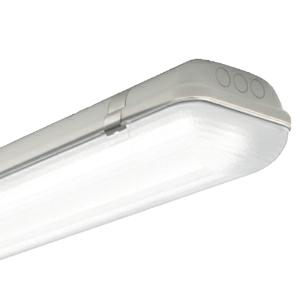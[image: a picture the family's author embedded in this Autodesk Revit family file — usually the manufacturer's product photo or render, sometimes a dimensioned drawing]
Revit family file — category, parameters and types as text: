
# Revit family: 3f_filippi_-_3f_linda_soft_3f_filippi_-_58754_-_3f_linda_led_soft_2x30w_dali_l1570
name_source: partatom
category: Lighting Fixtures
units: mm (PartAtom-declared; Revit-internal decimal feet)

## family parameters
Cut with Voids When Loaded = No
Host = Face
Light Source = No
Part Type = Normal
Room Calculation Point = No
Round Connector Dimension = Use Diameter
Shared = No

## types (1)
- 3F Filippi - 3F Linda Soft (1 x LED, 8788 lm, 66 W, 4000 K)
    Apparent Load = 66 VA
    Approval mark = CE
    CIE Flux Codes = 42 72 91 93 100
    Color Rendering = 80
    Color Temperature = 4000 K
    Control Gear = Electronic transformer
    Default Elevation = 1800 mm
    Description = ILLUMINOTECHNICAL
Luminous efficiency 100% (DLOR 93%, ULOR 7%).
Initial luminous flux of the luminaire 8788 lm.
Direct symmetric distribution.
Installation Interdistance Transv.D = 1.35 x hu - Long.D = 1.24 x hu.
Tabular UGR (CIE 117 - 4H-8H; S=0.25H; 70/50/20): RUG 24.5 - 22.7.
Beam angle: 131° - 111°.
Luminous efficacy 133 lm/W.
Lifetime (L93/B10): 30000 h. (tq+25°C)
Lifetime (L90/B10): 50000 h. (tq+25°C)
Lifetime (L85/B10): 80000 h. (tq+25°C)
Lifetime (L80/B10): 100000 h. (tq+25°C)
Lifetime (L85/B10): 50000 h. (tq+35°C)
Sudden decreased luminous flux after 50000 hours: 0% (C0).
Photobiological safety in compliance with IEC/TR 62778: RG0 risk exempt, (IEC 62471).
In compliance with IEC/EN 62722-2-1 - IEC/EN 62717 standards.

SOURCE
2 linear LED modules 30W/840.
Energy efficiency class (UE 2019/2020 - UE 2019/2015): D.
CIE 13.3 Colour rendering index: CRI >80 (R9 <50%).
IES TM-30 Fidelity Index: Rf = 84 Rg = 95.
CCT nominal colour temperature 4000 K.
Colour initial tolerance (MacAdam): SDCM 3.

MECHANICAL
Self-extinguishing V2 polycarbonate housing, injection moulded, RAL 7035 grey.
Ecologic anti-aging injected sealing gasket.
Soft opal diffuser in self-extinguishing V2 polycarbonate, photo-engraved interior, UV stabilised, injection moulded.
Gear-holder reflector in hot-dip galvanised steel, painted with white polyester base.
Snug fit safety snap-lock clips for diffuser mounting in stainless steel, screwdriver opening.
Fixing brackets in stainless steel.
Possibility for technicians to access the interior of the luminaire.
Luminaire with limited surface temperature. - D - (EN 60598-2-24)
Dimensions: 1570x160 mm, height 100 mm. Weight 3.35 kg.
IP66 protection degree.
Mechanical strength to impacts IK10 (20 joule).
Glow-wire test resistance 850°C.

ELECTRICAL
Halogen Free DALI-2 DATI (Parts 251, 252, 253), PUSH-DIM, electronic wiring 230V-50/60Hz, power factor 0.97 at full load, THD <25%, constant output current, SELV, class I, 1 driver, 1 DALI addresse.
Power of the luminaire 66 W.
ENEC - CE.
SAFE FLICKER: PstLM=<1 and SVM=<0.4 (IEC TR 61547-1 and IEC TR 63158), to ensure a more comfortable and safe light.
Luminaire compliant with EN 60598-2-22 for power supply from a centralised emergency system CPSS (Central Power Supply System), not incorporated in the luminaire - high risk areas excluded. The default power and flux are 100% in AC and 15% in DC.
Ambient temperature from -20°C to +35°C.
Temperature class T6 max 85°C.
Relative humidity UR: <85%.

INSTALLATION
Ceiling / Suspended / Wall.
All accessories dedicated to this product are available on the Catalog and on our website www.3F-Filippi.com.

APPLICATIONS
Suitable product for food production plants (HACCP), IFS (Food Version 6), BRC (GSFS Food Version 7).
Dry, dusty indoor environments, subject to occasional water splashes.
Luminaires designed for diffuse direct/indirect lighting suitable to provide optimum visual comfort.
Transit areas, stairwells.
Virtually shatterproof polycarbonate compatibly with the fumes / atmospheres that compromise the elasticity of plastic materials.
Suitable for illumination of public car parks and parking grounds referred to DIN 67528:2018-04.

LIGHT MANAGEMENT
Recommended minimum setting: 10%.
The luminaire, equipped with (DALI-2 DATI) driver, can be controlled manually with 3F Easy Dim technology or automatically/manually with wired or wireless DALI/D2D control systems.
The D2D driver guarantees interoperability with other devices with the same certification by making the following information available:
Device Data (Part 251), Energy Report (Part 252), Diagnosis & Maintenance (Part 253).
In electrical systems without a regulation system (manual or automatic) and DALI bus, a suitable jumper must be made on the DA-DA terminals of the appliance.

WARNING
Fixture not suitable for cold stores with an ambient temperature <0°C and/or relative humidity >85%.
Luminaire designed for disposal/recycling at end-of-life.
Replaceable (LED only) light source by a professional. Replaceable control gear by a professional.
    Height = 100 mm  [stored 0.328084 ft]
    Lamp = 1 x LED
    Lamp Light Flux = 8788 lm
    Lamp Power = 66 W
    Lamp count = 1
    Length = 1570 mm
    Lifetime = 50000 h
    Luminous efficacy = 133 lm/W
    Manufacturer = 3F Filippi
    ModVariant = No
    Model = 3F Filippi - 58754 - 3F Linda LED Soft 2x30W DALI L1570
    Mounting Place = Ceiling
    Mounting Type = Pendant
    Number of Poles = 1
    OnlyDefault = Yes
    Power Factor = 1
    Product Name = 3F Filippi - 3F Linda Soft
    Product group = pendant luminaire
    ProductGroupID = 9
    Protection Class = Protection class I
    Protection Degree = IP 66
    RLX_Detail_Level = 1
    RLX_Emergency_Light_Flux = 0 lm
    RLX_Emergency_Type = 0
    RLX_Emergency_Type_DB = No
    RlxData = <blob elided: 71649 chars, md5=aba5016e>
    Socket = socket
    Standby Power = 0 W
    System Light Flux = 8788 lm
    System Power = 66 W
    Type Comments = Product without accessories
    Type Image = 3ffilippi_3f_linda_led_soft_2x.jpg
    URL = http://relux.com
    VarID = ---
    Voltage = 0 V
    Weight = 0.00 kg
    Width = 160 mm

note: [stored X ft] marks values corroborated as IEEE doubles in the binary element streams (Revit-internal decimal feet)

## geometry (parser evidence)
native form markers: Blend x4, Sweep x12
no freeform markers — native parametric forms only
